# Revit family: Дверь МДО1
name_source: partatom
category: Двери
revit_build: Autodesk Revit 2015 (Build: 20140223_1515(x64)
units: mm (PartAtom-declared; Revit-internal decimal feet)

## types (1)
- Дверь МДО1
    ADSK_URL страницы изделия = http://profholod.ru
    ADSK_Завод-изготовитель = ООО ПрофХолод
    ADSK_Наименование = МДО 1000 2000 40 AISI 430-0,5 RAL - 0,5 0 Н Лев
    ADSK_Обозначение = ООО ПрофХолод
    ADSK_Открывание = Пр
    H_hole_bottom = 1300 мм
    H_hole_height = 580 мм
    URL = http://profholod.ru
    Аналитическая конструкция = <Нет>
    Внутренняя сторона = AISI 430-0,5
    Высота = 2100 мм
    Высота в свету = 2070 мм
    Высота порога = 0 мм
    Высота проема до монтажа = 2100 мм
    Группа модели = МДО
    Замыкание стены = По основе
    Изготовитель = ООО ПрофХолод
    Изогнутый отбойник левый = Нет
    Изогнутый отбойник правый = Да
    Иллюминатор высота = 580 мм
    Иллюминатор низ = 1300 мм
    Иллюминатор радиус = 150 мм
    Иллюминатор стекло = Пластмасса, прозрачная
    Коробка и наличники = RAL9003
    Наружная сторона = RAL9003
    Обхват = ТР : В обхват
    Описание = Двери маятниковые одностворчатые (МДО)
    Петли левые = Нет
    Петли правые = Да
    Плоский отбойник = Нет
    Побр = ТР : П-рама
    Резиновые изделия = Резина
    ТК_КРК = ККС : КРК - к крипичной стене
    ТК_МК = ККС : МК - к металлоконструкции
    ТК_СП = ККС : СП - к сэндвич-панели
    Температурный режим = C
    Тип отбойника = Изогнутый отбойник
    Толщина полотна = 40 мм
    Угол = ТР : Угловая рама
    Функция = Внутренние слои
    Ширина = 1100 мм
    Ширина в свету = 874 мм
    Ширина проема до монтажа = 1100 мм

## geometry (parser evidence)
native form markers: Sweep x5
no freeform markers — native parametric forms only
